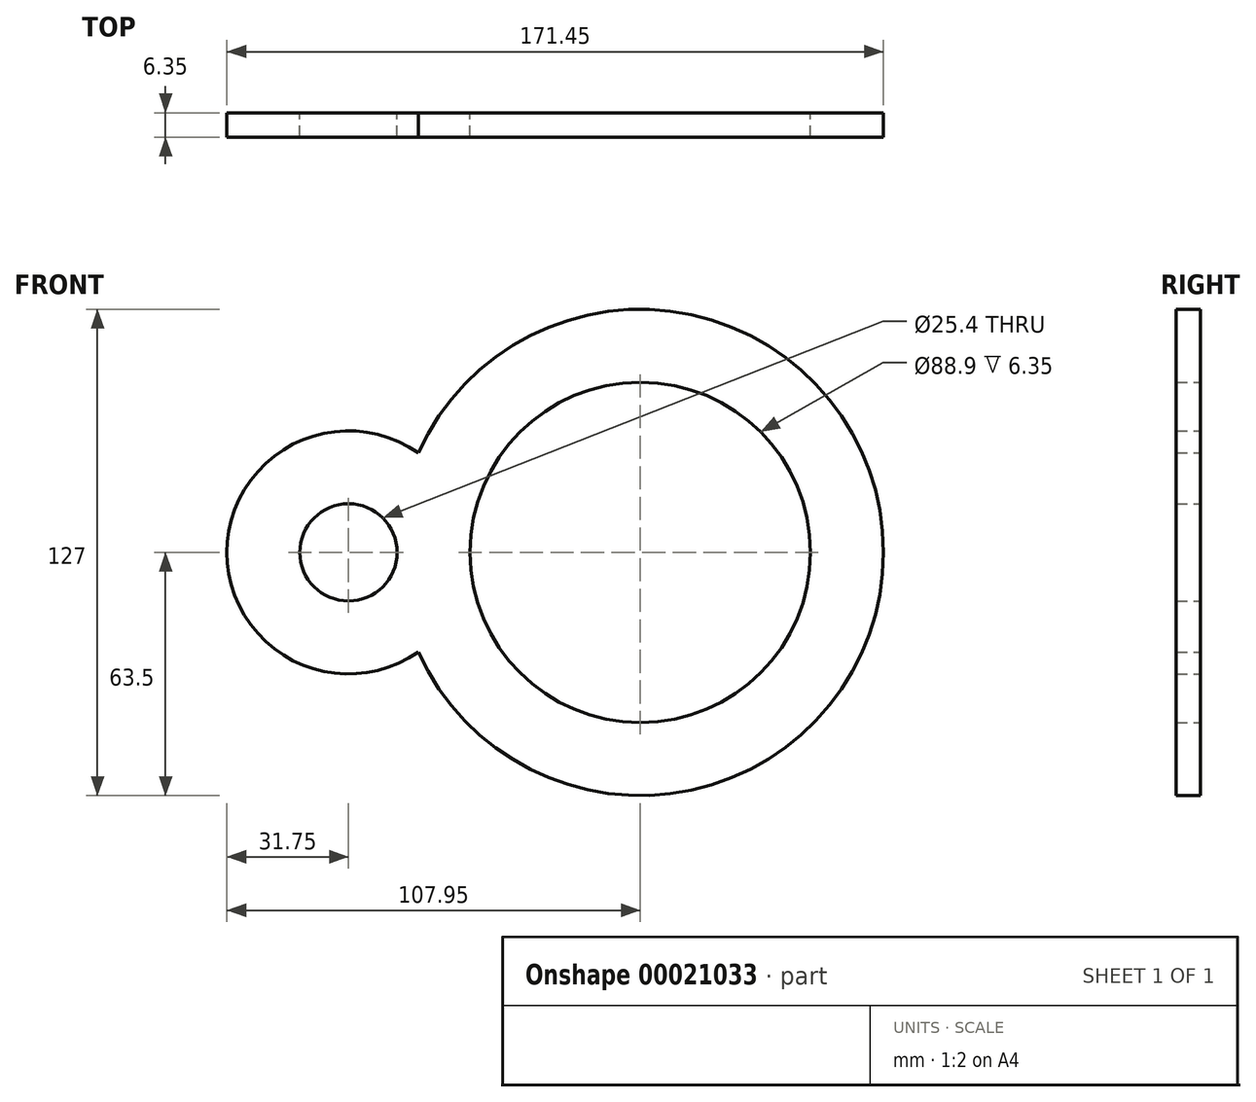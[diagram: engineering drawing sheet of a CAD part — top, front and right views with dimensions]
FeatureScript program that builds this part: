
annotation { "Feature Type Name" : "Feature", "Feature Type Description" : "" }
export const myFeature = defineFeature(function(context is Context, id is Id, definition is map)
    precondition{}
    {
        {
            var Q0;
            Q0=qCreatedBy(makeId("Front.planeOp"),FACE);
            var sketch = newSketch(context, id + "F0", { "sketchPlane" : qUnion([Q0])});
            skCircle(sketch, "E0", {"center": v(0, 0) * mm, "radius": 44.45 * mm});
            skCircle(sketch, "E1", {"center": v(76.2, 0) * mm, "radius": 12.7 * mm});
            skCircle(sketch, "E2", {"center": v(-76.2, 0) * mm, "radius": 12.7 * mm});
            skArc(sketch, "E3", {"start": v(-57.94, 25.98) * mm, "mid": v(-107.95, 0) * mm, "end": v(-57.94, -25.98) * mm});
            skLineSegment(sketch, "E4", {"start": v(57.94, 25.98) * mm, "end": v(57.94, 25.98) * mm});
            skArc(sketch, "E5", {"start": v(-57.94, -25.98) * mm, "mid": v(25.98, -57.94) * mm, "end": v(57.94, 25.98) * mm});
            skArc(sketch, "E6.trimOffspring", {"start": v(57.94, 25.98) * mm, "mid": v(0, 63.5) * mm, "end": v(-57.94, 25.98) * mm});
            skSolve(sketch);
        }
        {
            var Q0;
            Q0=makeQuery(id+"F0.imprint","IMPRINT",FACE,{"disambiguationData":[TD([[makeQuery(id+"F0.imprint","IMPRINT",EDGE,{"derivedFrom":sQuery(id+"F0.wireOp",EDGE,"E0")}),-1.0]])]});
            extrude(context, id + "F1", {"entities" : qUnion([Q0]), "depth" : 6.35 * mm});
        }
    });
